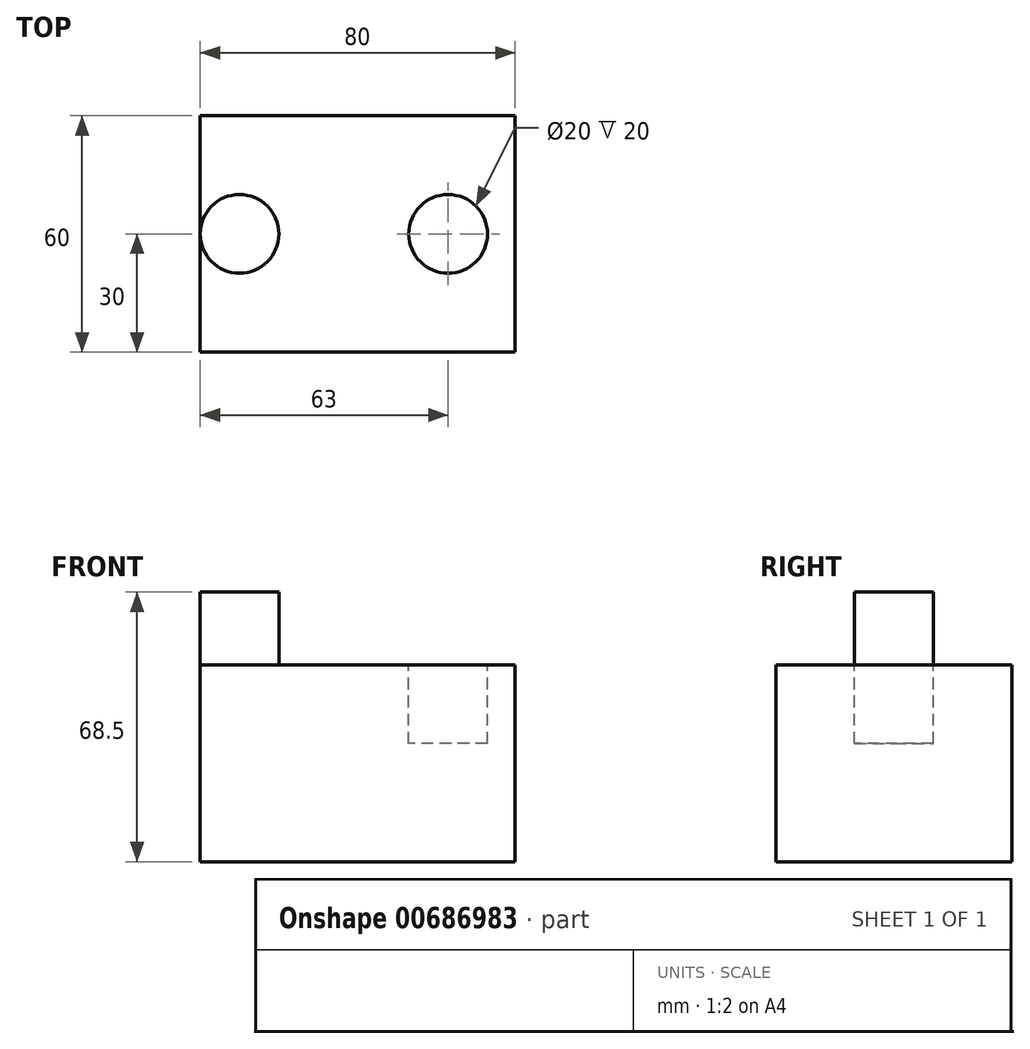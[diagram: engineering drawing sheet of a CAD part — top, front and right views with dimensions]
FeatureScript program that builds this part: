
annotation { "Feature Type Name" : "Feature", "Feature Type Description" : "" }
export const myFeature = defineFeature(function(context is Context, id is Id, definition is map)
    precondition{}
    {
        {
            var Q0;
            Q0=qCreatedBy(makeId("Top.planeOp"),FACE);
            var sketch = newSketch(context, id + "F0", { "sketchPlane" : qUnion([Q0])});
            skLineSegment(sketch, "E0.bottom", {"start": v(40, 30) * mm, "end": v(-40, 30) * mm});
            skLineSegment(sketch, "E0.top", {"start": v(40, -30) * mm, "end": v(-40, -30) * mm});
            skLineSegment(sketch, "E0.left", {"start": v(40, 30) * mm, "end": v(40, -30) * mm});
            skLineSegment(sketch, "E0.right", {"start": v(-40, 30) * mm, "end": v(-40, -30) * mm});
            skPoint(sketch, "E0.middle", {"position": v(0, 0) * mm});
            skSolve(sketch);
        }
        {
            var Q0;
            Q0=makeQuery(id+"F0.imprint","IMPRINT",FACE,{"disambiguationData":[TD([[makeQuery(id+"F0.imprint","IMPRINT",EDGE,{"derivedFrom":sQuery(id+"F0.wireOp",EDGE,"E0.bottom")}),1.0]])]});
            var Q1;
            Q1 = qSketchRegion(id + "F0", true);
            extrude(context, id + "F1", {"entities" : qUnion([Q0, Q1]), "depth" : 50 * mm, "offsetDistance" : 25 * mm});
        }
        {
            var Q0;
            Q0=makeQuery(id+"F1.opExtrude","CAP_FACE",FACE,{"disambiguationData":[OSD([sQuery(id+"F0.wireOp",EDGE,"E0.bottom"),sQuery(id+"F0.wireOp",EDGE,"E0.top"),sQuery(id+"F0.wireOp",EDGE,"E0.left"),sQuery(id+"F0.wireOp",EDGE,"E0.right")])],"isStart":false});
            var sketch = newSketch(context, id + "F2", { "sketchPlane" : qUnion([Q0])});
            skCircle(sketch, "E1", {"center": v(-30, 0) * mm, "radius": 10 * mm});
            skSolve(sketch);
        }
        {
            var Q0;
            Q0 = qSketchRegion(id + "F2", true);
            extrude(context, id + "F3", {"entities" : qUnion([Q0]), "operationType" : NewBodyOperationType.ADD, "depth" : 18.5 * mm, "offsetDistance" : 25 * mm});
        }
        {
            var Q0;
            Q0=makeQuery(id+"F1.opExtrude","CAP_FACE",FACE,{"disambiguationData":[OSD([sQuery(id+"F0.wireOp",EDGE,"E0.bottom"),sQuery(id+"F0.wireOp",EDGE,"E0.top"),sQuery(id+"F0.wireOp",EDGE,"E0.left"),sQuery(id+"F0.wireOp",EDGE,"E0.right")])],"isStart":false});
            var sketch = newSketch(context, id + "F4", { "sketchPlane" : qUnion([Q0])});
            skCircle(sketch, "E2", {"center": v(23, 0) * mm, "radius": 10 * mm});
            skSolve(sketch);
        }
        {
            var Q0;
            Q0 = qSketchRegion(id + "F4", true);
            extrude(context, id + "F5", {"entities" : qUnion([Q0]), "operationType" : NewBodyOperationType.REMOVE, "oppositeDirection" : true, "depth" : 20 * mm, "offsetDistance" : 25 * mm});
        }
    });
